# Revit family: Haworth_JiveTable_Rectangle_XBase NEW
name_source: partatom
category: Furniture Systems
revit_build: Autodesk Revit 2018 (Build: 20170223_1515(x64)
units: mm (PartAtom-declared; Revit-internal decimal feet)

## family parameters
Always vertical = Yes
Cut with Voids When Loaded = No
OmniClass Number = 23.40.70.14.64.21
OmniClass Title = Systems Furniture
Part Type = Normal
Room Calculation Point = No
Round Connector Dimension = Use Diameter
Shared = No
Work Plane-Based = No

## types (1)
- 42d 42w 29h - X Base - With Casters
    2 Column = No
    3 Column = No
    6 Column = No
    8 Column = No
    Actual Casters = Yes
    Actual Depth = 42"
    Actual Glide = No
    Actual Height = 29"
    Actual Table Depth = 48"
    Actual Table Width = 48"
    Actual Width = 42"
    Assembly Code = E2020200
    Bridge Distance = 24"
    Casters = Yes
    Center Leg Location = 0"
    Columns = No
    Custom Size = No
    Depth = 42"
    Description = Haworth Jive Table Rectangle Bases - 224d 36w 29h - X Base - With Casters
    Glides = No
    Height = 29"
    Leg Height = 27 13/16"
    Manufacturer = Haworth, Inc.
    Max. Depth = 42"
    Max. Height = 42"
    Max. Width = 42"
    Middle Columns = No
    Min. Depth = 24"
    Min. Height = 16"
    Min. Width = 24"
    Model = Haworth Jive
    Revision Number = 1
    Size = Verify Final Dim. w/ Haworth
    Standard Depths = 30, 36, 42 in.
    Standard Heights = 16, 20, 29, 36, 42 in.
    Standard Widths = 24, 30 in.
    Support Depth 6 8 Column = 10 29/32"
    Support Distance 6 8 Column = 10 29/32"
    Table Thickness = 1 3/16"
    URL = http://www.haworth.com
    URL - Product = http://www.haworth.com
    Warranty = http://www.haworth.com
    Width = 42"

## geometry (parser evidence)
native form markers: Sweep x15
no freeform markers — native parametric forms only
